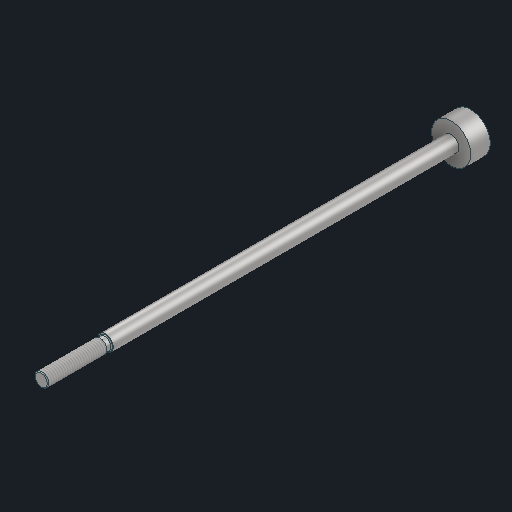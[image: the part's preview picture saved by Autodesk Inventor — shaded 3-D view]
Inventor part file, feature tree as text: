
AUTODESK INVENTOR PART (.ipt)
format: ipt  version: 2024 (Build 280153000, 153)  size: 125,440 bytes
history: native  units: in
note: dims shown in document units (in); Inventor stores cm internally (conversion verified against a paired STEP export)
features: thread x2
ambient origin geometry x8: Origin, YZ Plane, XZ Plane, XY Plane, X Axis, Y Axis, Z Axis, Center Point
bodies: Solid1 (feature_tree)
feature tree (2):
  thread  "Thread1"  [1 undecoded]
  thread  "Threads"  [1 undecoded]
note: 2 required parameter values undecoded (feature->parameter linkage not recoverable at this tier; creation-order binding heuristic only, values carry confidence <= 0.55)
